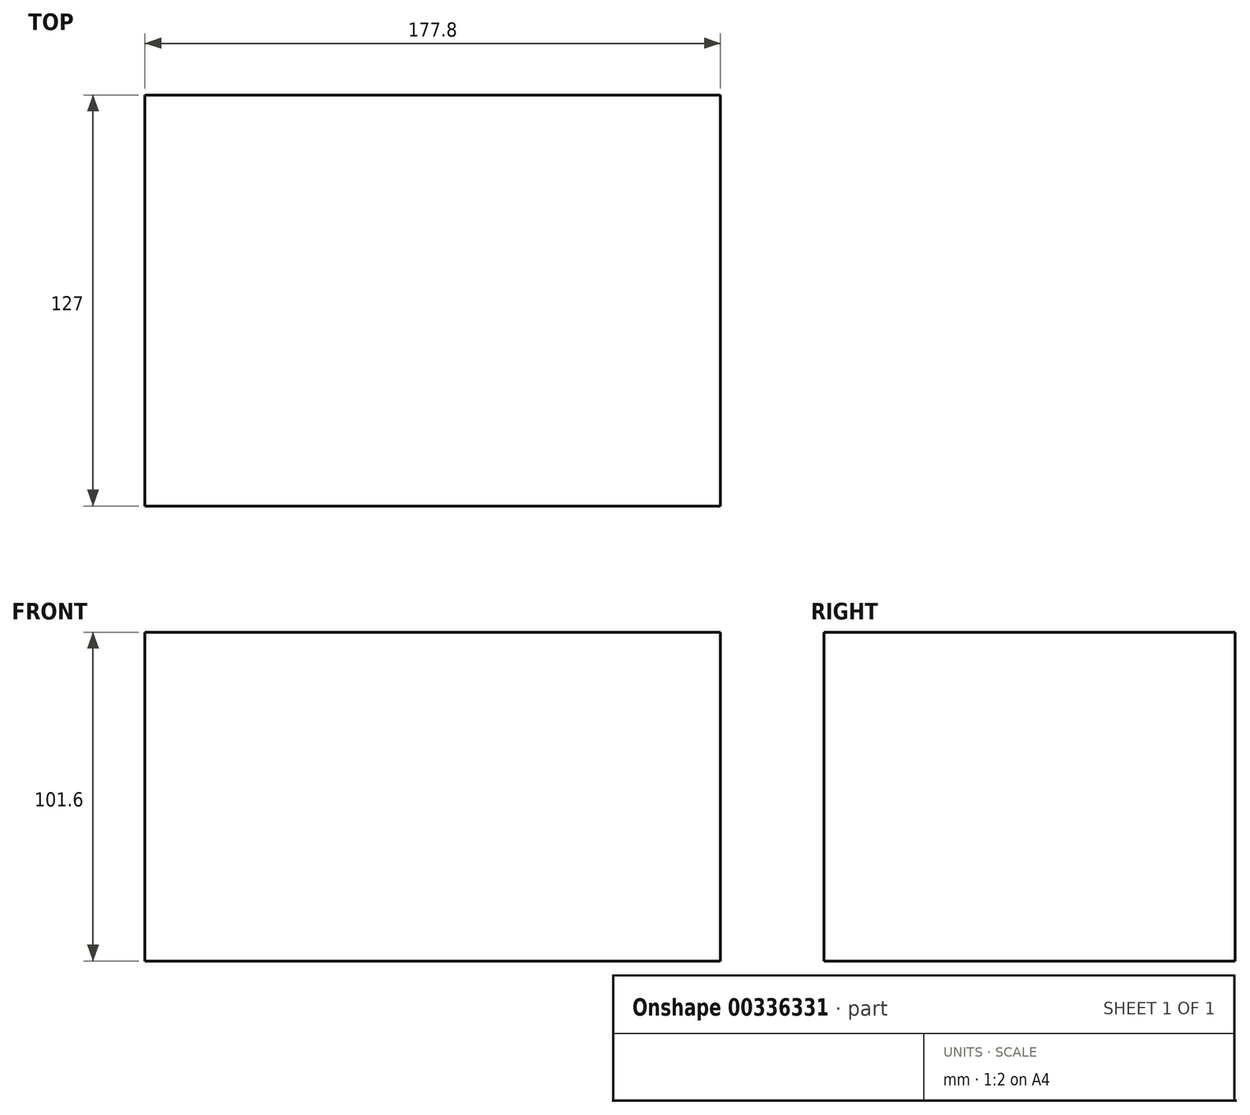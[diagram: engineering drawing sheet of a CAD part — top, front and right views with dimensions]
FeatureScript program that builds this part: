
annotation { "Feature Type Name" : "Feature", "Feature Type Description" : "" }
export const myFeature = defineFeature(function(context is Context, id is Id, definition is map)
    precondition{}
    {
        {
            var Q0;
            Q0=qCreatedBy(makeId("Top.planeOp"),FACE);
            var sketch = newSketch(context, id + "F0", { "sketchPlane" : qUnion([Q0])});
            skLineSegment(sketch, "E0.bottom", {"start": v(-94.06, -56.7) * mm, "end": v(83.74, -56.7) * mm});
            skLineSegment(sketch, "E0.top", {"start": v(-94.06, 70.3) * mm, "end": v(83.74, 70.3) * mm});
            skLineSegment(sketch, "E0.left", {"start": v(-94.06, -56.7) * mm, "end": v(-94.06, 70.3) * mm});
            skLineSegment(sketch, "E0.right", {"start": v(83.74, -56.7) * mm, "end": v(83.74, 70.3) * mm});
            skSolve(sketch);
        }
        {
            var Q0;
            Q0 = qSketchRegion(id + "F0", true);
            extrude(context, id + "F1", {"entities" : qUnion([Q0]), "depth" : 101.6 * mm});
        }
    });
